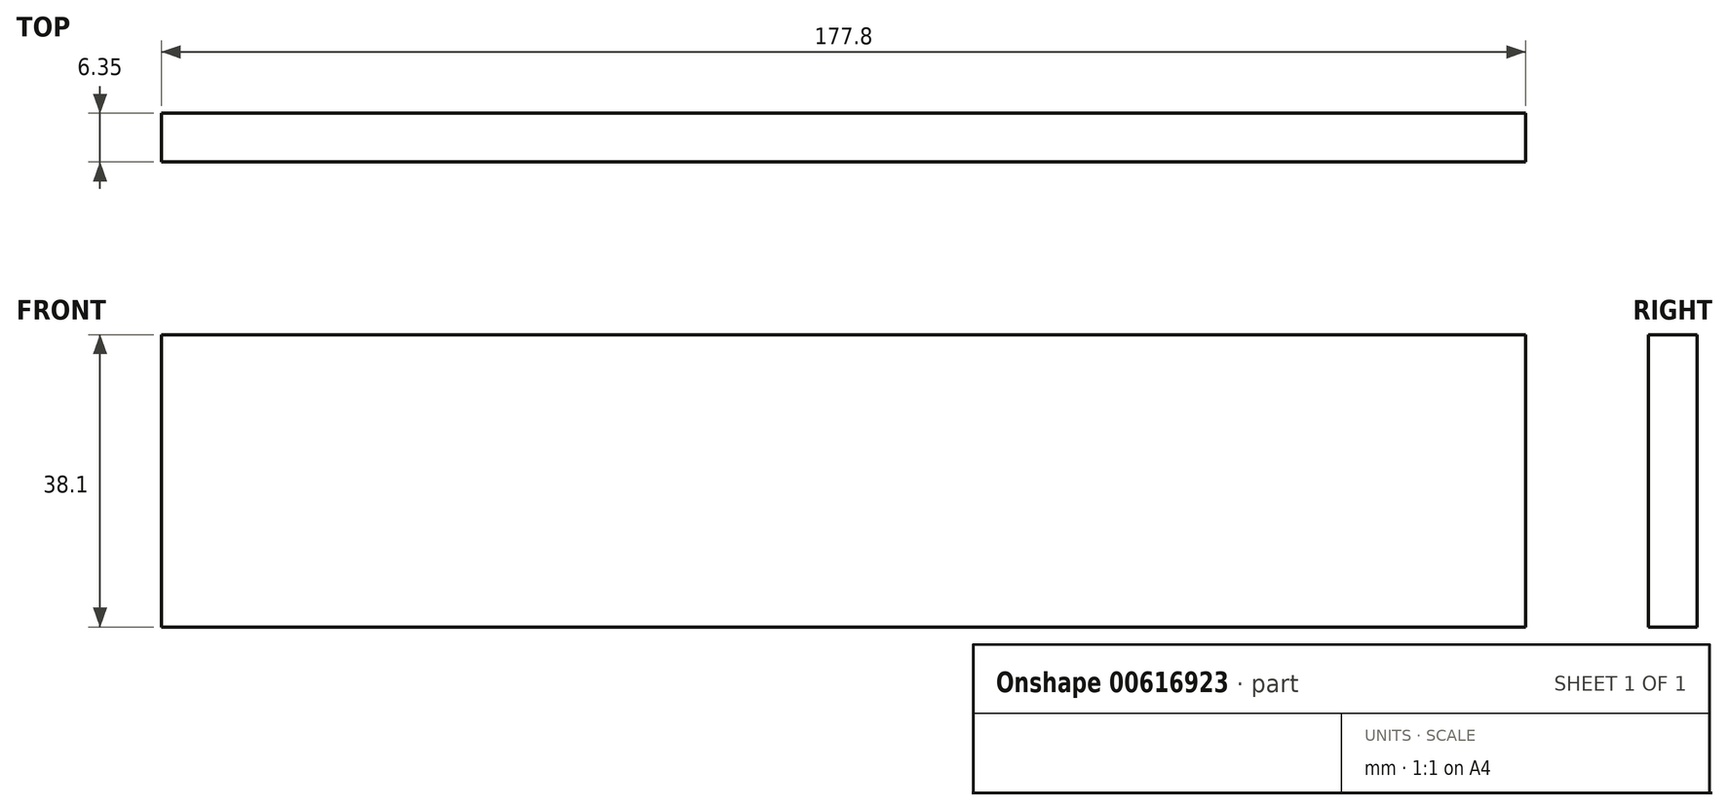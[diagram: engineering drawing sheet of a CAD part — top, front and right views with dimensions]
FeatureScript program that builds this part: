
annotation { "Feature Type Name" : "Feature", "Feature Type Description" : "" }
export const myFeature = defineFeature(function(context is Context, id is Id, definition is map)
    precondition{}
    {
        {
            var Q0;
            Q0=qCreatedBy(makeId("Front.planeOp"),FACE);
            var sketch = newSketch(context, id + "F0", { "sketchPlane" : qUnion([Q0])});
            skLineSegment(sketch, "E0", {"start": v(-88.9, 0) * mm, "end": v(88.9, 0) * mm});
            skLineSegment(sketch, "E1", {"start": v(88.9, 0) * mm, "end": v(88.9, 38.1) * mm});
            skLineSegment(sketch, "E2", {"start": v(88.9, 38.1) * mm, "end": v(-88.9, 38.1) * mm});
            skLineSegment(sketch, "E3", {"start": v(-88.9, 38.1) * mm, "end": v(-88.9, 0) * mm});
            skSolve(sketch);
        }
        {
            var Q0;
            Q0=makeQuery(id+"F0.imprint","IMPRINT",FACE,{"disambiguationData":[TD([[makeQuery(id+"F0.imprint","IMPRINT",EDGE,{"derivedFrom":sQuery(id+"F0.wireOp",EDGE,"E0")}),1.0]])]});
            extrude(context, id + "F1", {"entities" : qUnion([Q0]), "depth" : 6.35 * mm, "offsetDistance" : 25.4 * mm});
        }
    });
